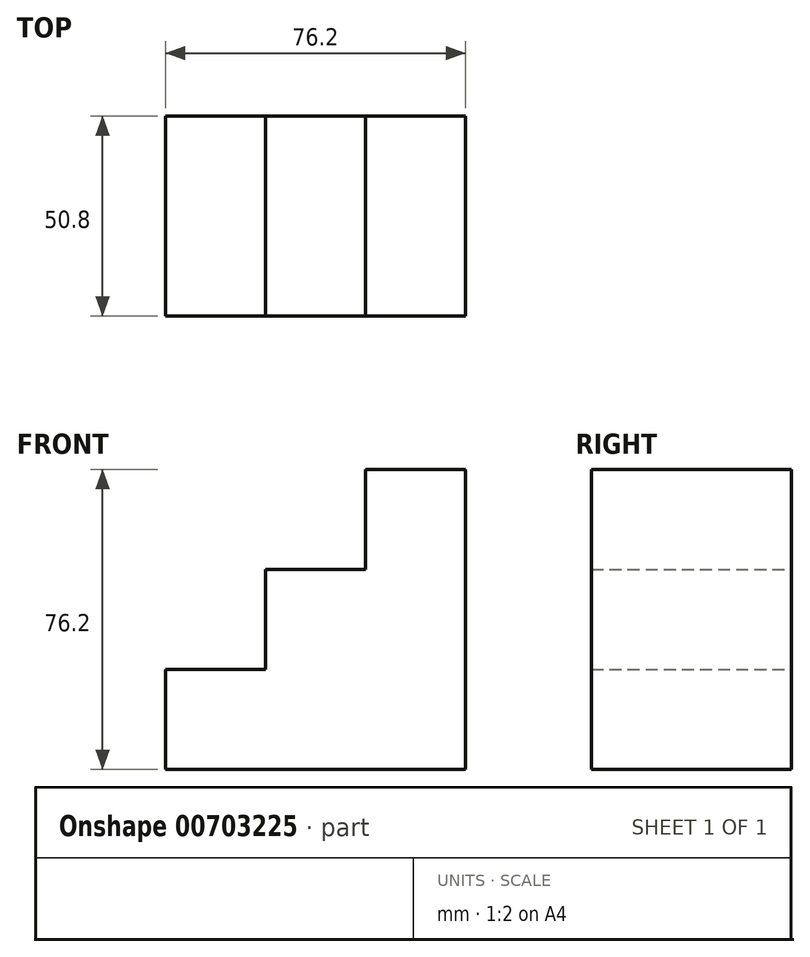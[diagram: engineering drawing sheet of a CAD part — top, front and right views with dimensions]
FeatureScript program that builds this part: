
annotation { "Feature Type Name" : "Feature", "Feature Type Description" : "" }
export const myFeature = defineFeature(function(context is Context, id is Id, definition is map)
    precondition{}
    {
        {
            var Q0;
            Q0=qCreatedBy(makeId("Front.planeOp"),FACE);
            var sketch = newSketch(context, id + "F0", { "sketchPlane" : qUnion([Q0])});
            skLineSegment(sketch, "E0", {"start": v(-37.71, -18.43) * mm, "end": v(38.49, -18.43) * mm});
            skLineSegment(sketch, "E1", {"start": v(38.49, -18.43) * mm, "end": v(38.49, 57.77) * mm});
            skLineSegment(sketch, "E2", {"start": v(38.49, 57.77) * mm, "end": v(13.09, 57.77) * mm});
            skLineSegment(sketch, "E3", {"start": v(13.09, 57.77) * mm, "end": v(13.09, 32.37) * mm});
            skLineSegment(sketch, "E4", {"start": v(13.09, 32.37) * mm, "end": v(-12.31, 32.37) * mm});
            skLineSegment(sketch, "E5", {"start": v(-12.31, 32.37) * mm, "end": v(-12.31, 6.97) * mm});
            skLineSegment(sketch, "E6", {"start": v(-12.31, 6.97) * mm, "end": v(-37.71, 6.97) * mm});
            skLineSegment(sketch, "E7", {"start": v(-37.71, 6.97) * mm, "end": v(-37.71, -18.43) * mm});
            skSolve(sketch);
        }
        {
            var Q0;
            Q0 = qSketchRegion(id + "F0", true);
            extrude(context, id + "F1", {"entities" : qUnion([Q0]), "depth" : 50.8 * mm, "offsetDistance" : 25.4 * mm});
        }
    });
